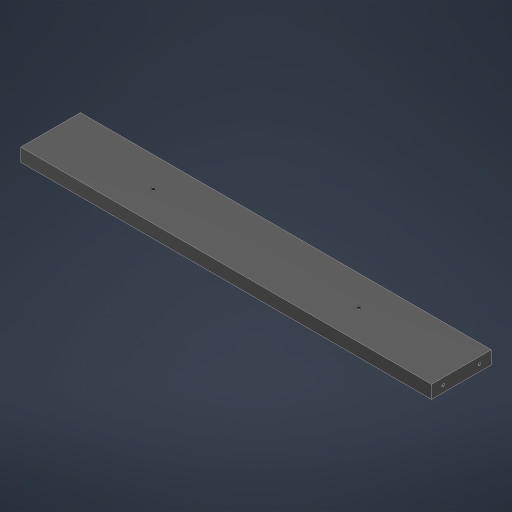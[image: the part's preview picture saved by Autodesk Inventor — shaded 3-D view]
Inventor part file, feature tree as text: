
AUTODESK INVENTOR PART (.ipt)
format: ipt  version: 2024 (Build 280153000, 153)  size: 215,040 bytes
history: native  units: in
note: dims shown in document units (in); Inventor stores cm internally (conversion verified against a paired STEP export)
features: other x1, extrude x1, sketch x1
ambient origin geometry x8: Origin, YZ Plane, XZ Plane, XY Plane, X Axis, Y Axis, Z Axis, Center Point
bodies: Body1 (feature_tree)
feature tree (3):
  other  "Sólido1"
  extrude  "Extrusión1"  Depth=0.7087in
  sketch  "Boceto1"  dims[d0=0.1575in d1=0.1575in d2=0.6299in d3=1.9685in d4=0.7087in d5=0.3543in d6=0.3543in d7=39.3701in d8=0.0in]
